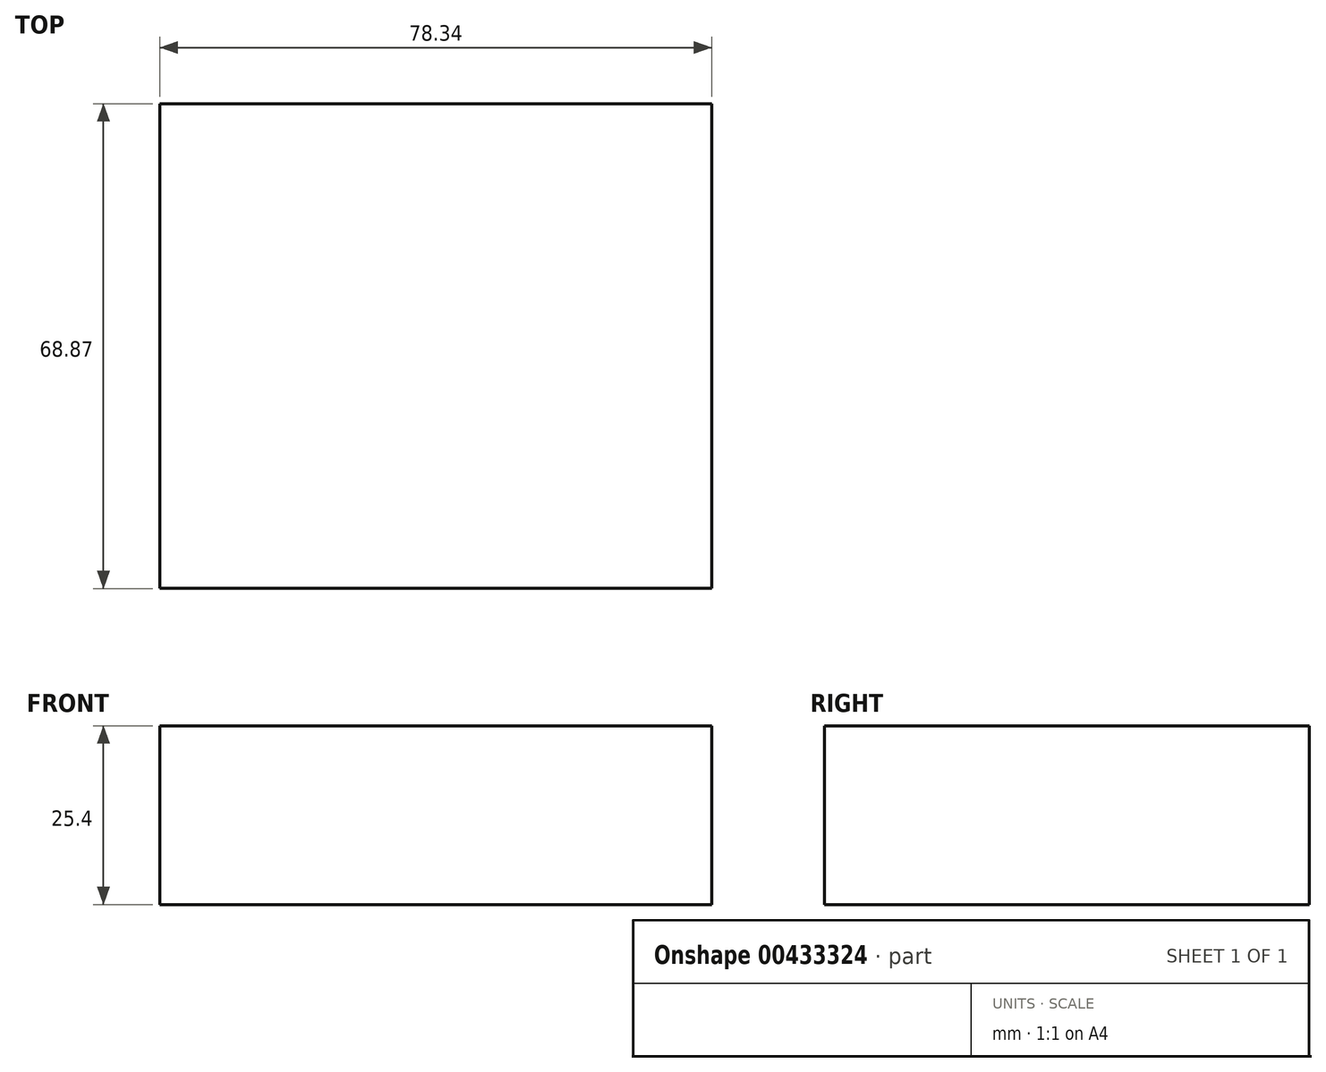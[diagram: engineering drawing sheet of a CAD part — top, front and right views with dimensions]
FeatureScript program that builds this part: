
annotation { "Feature Type Name" : "Feature", "Feature Type Description" : "" }
export const myFeature = defineFeature(function(context is Context, id is Id, definition is map)
    precondition{}
    {
        {
            var Q0;
            Q0=qCreatedBy(makeId("Top.planeOp"),FACE);
            var sketch = newSketch(context, id + "F0", { "sketchPlane" : qUnion([Q0])});
            skLineSegment(sketch, "E0.bottom", {"start": v(-64.9, 11.33) * mm, "end": v(13.43, 11.33) * mm});
            skLineSegment(sketch, "E0.top", {"start": v(-64.9, -57.54) * mm, "end": v(13.43, -57.54) * mm});
            skLineSegment(sketch, "E0.left", {"start": v(-64.9, 11.33) * mm, "end": v(-64.9, -57.54) * mm});
            skLineSegment(sketch, "E0.right", {"start": v(13.43, 11.33) * mm, "end": v(13.43, -57.54) * mm});
            skSolve(sketch);
        }
        {
            var Q0;
            Q0 = qSketchRegion(id + "F0", true);
            extrude(context, id + "F1", {"entities" : qUnion([Q0]), "depth" : 25.4 * mm});
        }
    });
